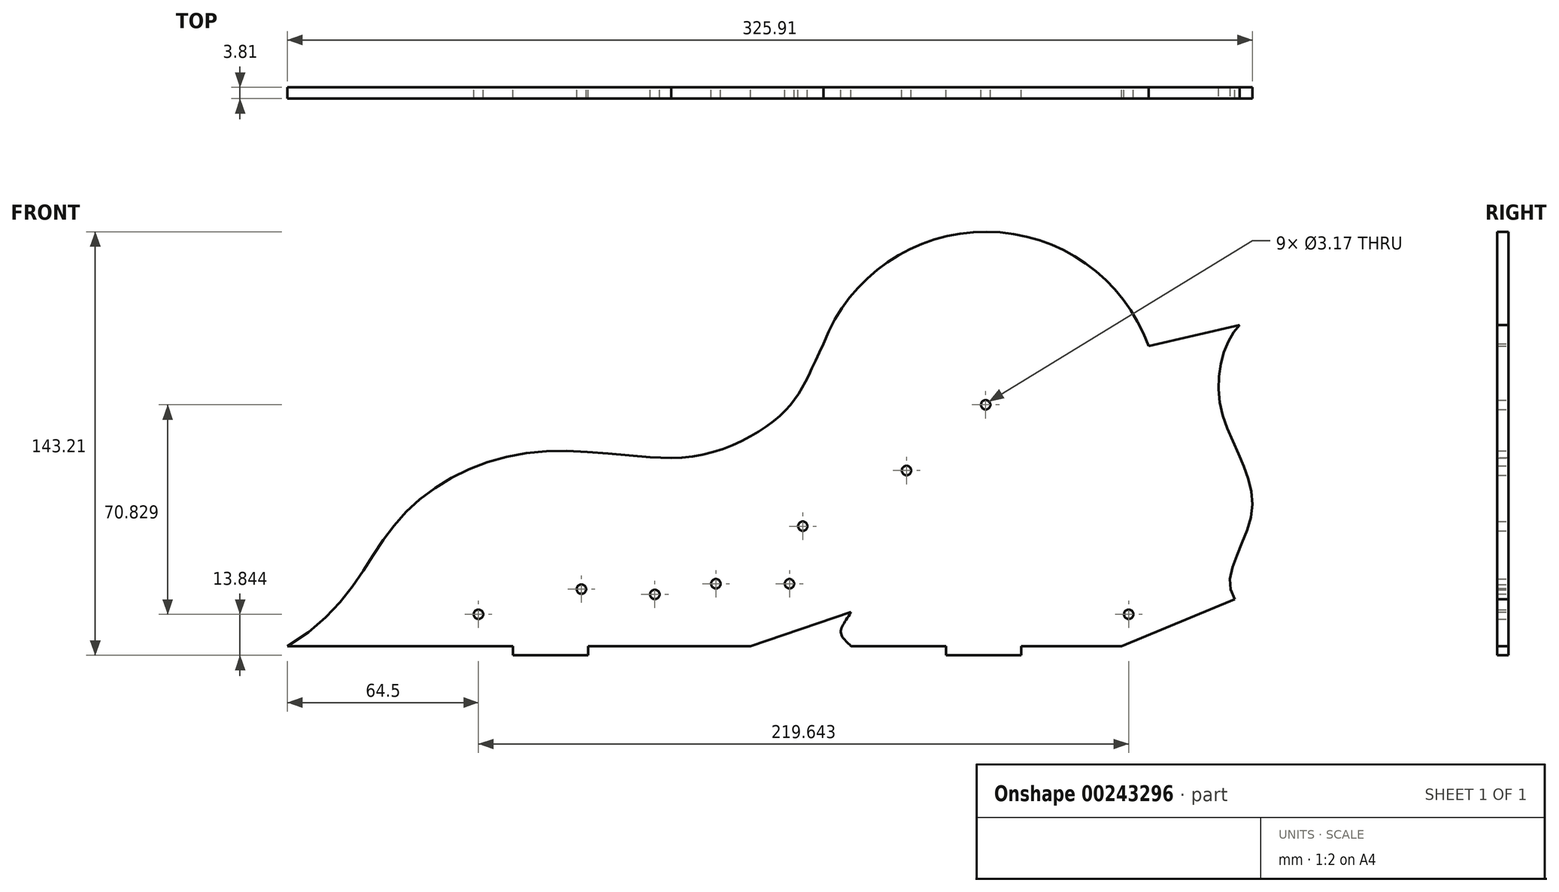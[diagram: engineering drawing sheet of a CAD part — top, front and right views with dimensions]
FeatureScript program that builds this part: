
annotation { "Feature Type Name" : "Feature", "Feature Type Description" : "" }
export const myFeature = defineFeature(function(context is Context, id is Id, definition is map)
    precondition{}
    {
        {
            var Q0;
            Q0=qCreatedBy(makeId("Front.planeOp"),FACE);
            var sketch = newSketch(context, id + "F0", { "sketchPlane" : qUnion([Q0])});
            skLineSegment(sketch, "E0.top", {"start": v(-43.1, 0) * mm, "end": v(11.74, 0) * mm});
            skCircle(sketch, "E1", {"center": v(29.36, 40.52) * mm, "radius": 1.59 * mm});
            skLineSegment(sketch, "E2", {"start": v(-144.7, 0) * mm, "end": v(-68.5, 0) * mm});
            skCircle(sketch, "E3", {"center": v(91.15, 81.55) * mm, "radius": 1.59 * mm});
            skCircle(sketch, "E4", {"center": v(64.4, 59.33) * mm, "radius": 1.59 * mm});
            skCircle(sketch, "E5", {"center": v(24.87, 21.07) * mm, "radius": 1.59 * mm});
            skCircle(sketch, "E6", {"center": v(0, 21.07) * mm, "radius": 1.59 * mm});
            skLineSegment(sketch, "E7", {"start": v(146.2, 101.45) * mm, "end": v(176.99, 108.58) * mm});
            skCircle(sketch, "E8", {"center": v(-20.61, 17.45) * mm, "radius": 1.59 * mm});
            skCircle(sketch, "E9", {"center": v(-45.42, 19.23) * mm, "radius": 1.59 * mm});
            skFitSpline(sketch, "E10", {"points": [v(42.71, 85.43) * mm, v(0, 64.34) * mm, v(-61.52, 65.57) * mm, v(-107.12, 42.69) * mm, v(-144.7, 0) * mm], "startDerivative": vector(-87.18, -109.32) * mm, "endDerivative": vector(-254.3, -148.83) * mm});
            skFitSpline(sketch, "E11", {"points": [v(176.99, 108.58) * mm, v(170.36, 81.6) * mm, v(181.09, 45.84) * mm, v(175.36, 15.8) * mm], "startDerivative": vector(-50.44, -50.2) * mm, "endDerivative": vector(52.78, -71.47) * mm});
            skLineSegment(sketch, "E12", {"start": v(175.36, 15.8) * mm, "end": v(137.1, 0) * mm});
            skLineSegment(sketch, "E13", {"start": v(45.62, 11.45) * mm, "end": v(11.74, 0) * mm});
            skFitSpline(sketch, "E14", {"points": [v(45.62, 11.45) * mm, v(42.23, 4.52) * mm, v(45.62, 0) * mm], "startDerivative": vector(-9.03, -15.75) * mm, "endDerivative": vector(9.75, -9.25) * mm});
            skLineSegment(sketch, "E15.trimOffspring", {"start": v(45.62, 0) * mm, "end": v(77.74, 0) * mm});
            skCircle(sketch, "E16", {"center": v(-80.19, 10.72) * mm, "radius": 1.59 * mm});
            skCircle(sketch, "E17", {"center": v(139.45, 10.72) * mm, "radius": 1.59 * mm});
            skArc(sketch, "E18", {"start": v(146.2, 101.45) * mm, "mid": v(91.53, 140.08) * mm, "end": v(36.37, 102.16) * mm});
            skPoint(sketch, "E19.startDerivative.orphan", {"position": v(5.5, 72.9) * mm});
            skPoint(sketch, "E20.1.internal.orphan", {"position": v(25.94, 72.9) * mm});
            skFitSpline(sketch, "E21", {"points": [v(-15.08, 63.52) * mm, v(23.06, 79.26) * mm, v(36.37, 102.16) * mm], "startDerivative": vector(83.27, -0.1) * mm, "endDerivative": vector(35.25, 70.94) * mm});
            skLineSegment(sketch, "E22.top", {"start": v(-68.5, -3.12) * mm, "end": v(-43.1, -3.12) * mm});
            skLineSegment(sketch, "E22.left", {"start": v(-68.5, 0) * mm, "end": v(-68.5, -3.12) * mm});
            skLineSegment(sketch, "E22.right", {"start": v(-43.1, 0) * mm, "end": v(-43.1, -3.12) * mm});
            skLineSegment(sketch, "E23.top", {"start": v(77.74, -3.12) * mm, "end": v(103.14, -3.12) * mm});
            skLineSegment(sketch, "E23.left", {"start": v(77.74, 0) * mm, "end": v(77.74, -3.12) * mm});
            skLineSegment(sketch, "E23.right", {"start": v(103.14, 0) * mm, "end": v(103.14, -3.12) * mm});
            skLineSegment(sketch, "E24.trimOffspring", {"start": v(103.14, 0) * mm, "end": v(137.1, 0) * mm});
            skLineSegment(sketch, "E25", {"start": v(91.15, 81.55) * mm, "end": v(64.4, 59.33) * mm});
            skLineSegment(sketch, "E26", {"start": v(64.4, 59.33) * mm, "end": v(29.36, 40.52) * mm});
            skSolve(sketch);
        }
        {
            var Q0;
            Q0=qSketchRegion(id+"F0",true);
            extrude(context, id + "F1", {"entities" : qUnion([Q0]), "depth" : 3.8 * mm});
        }
    });
